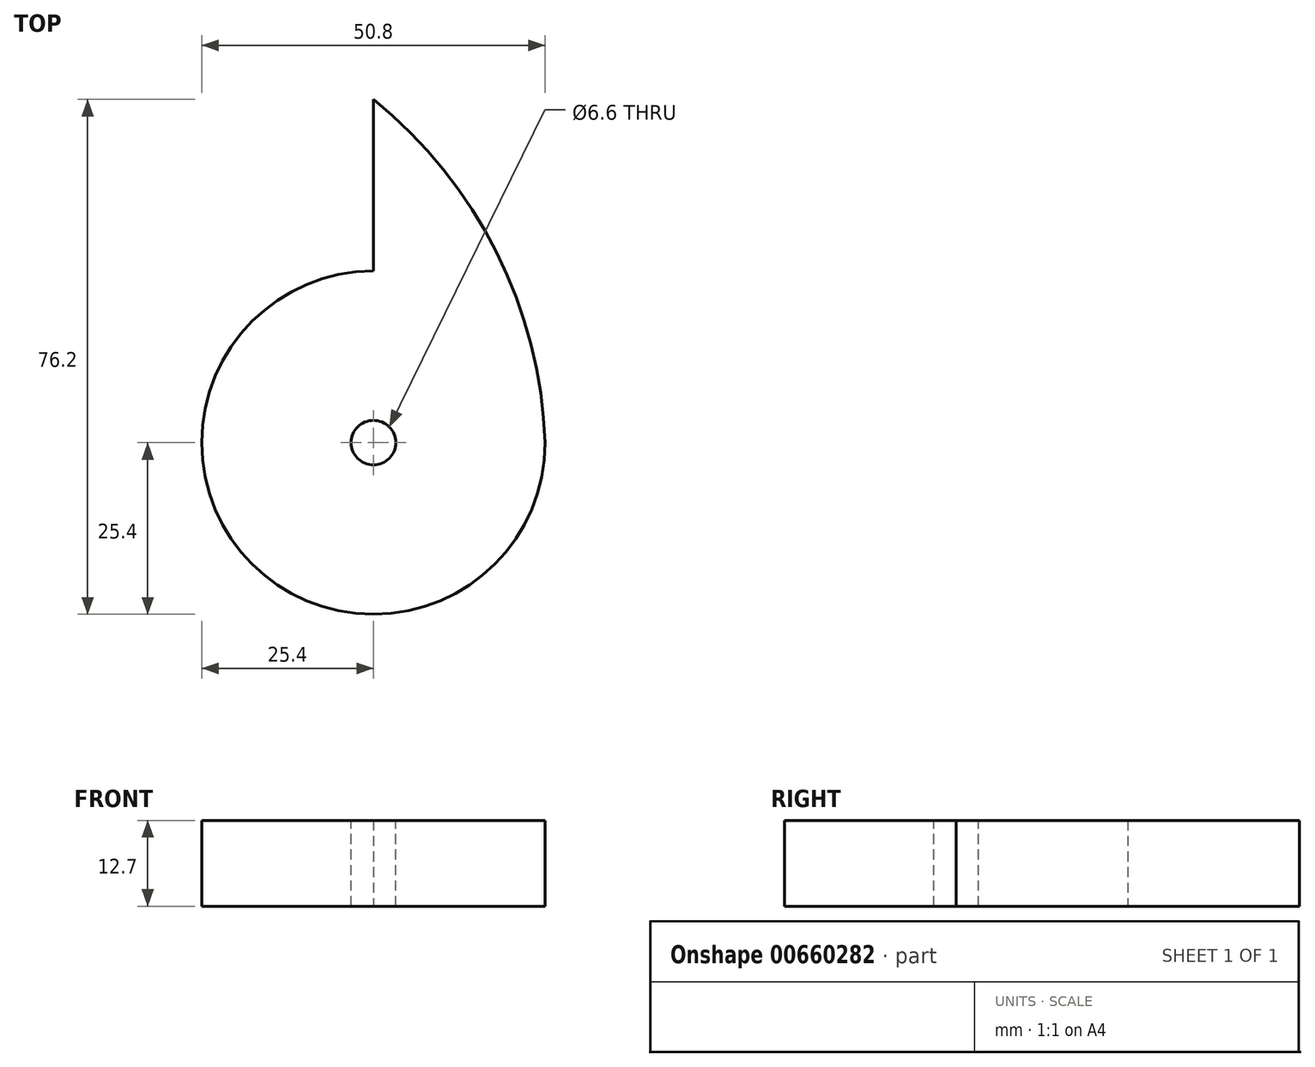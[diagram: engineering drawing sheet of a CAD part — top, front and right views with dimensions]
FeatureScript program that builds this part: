
annotation { "Feature Type Name" : "Feature", "Feature Type Description" : "" }
export const myFeature = defineFeature(function(context is Context, id is Id, definition is map)
    precondition{}
    {
        {
            var Q0;
            Q0=qCreatedBy(makeId("Top.planeOp"),FACE);
            var sketch = newSketch(context, id + "F0", { "sketchPlane" : qUnion([Q0])});
            skCircle(sketch, "E0", {"center": v(0, 0) * mm, "radius": 25.4 * mm});
            skLineSegment(sketch, "E1", {"start": v(0, 25.4) * mm, "end": v(0, 50.8) * mm});
            skArc(sketch, "E2", {"start": v(25.4, 0) * mm, "mid": v(18.21, 28.16) * mm, "end": v(0, 50.8) * mm});
            skSolve(sketch);
        }
        {
            var Q0;
            {var subQ0=sQuery(id+"F0.wireOp",EDGE,"E0");var subQ1=makeQuery(id+"F0.imprint","INTERSECT",VERTEX,{"derivedFrom":[subQ0,sQuery(id+"F0.wireOp",EDGE,"E1")]});Q0=makeQuery(id+"F0.imprint","IMPRINT",FACE,{"disambiguationData":[TD([[makeQuery(id+"F0.imprint","IMPRINT",EDGE,{"disambiguationData":[TD([[subQ1,1.0]])],"derivedFrom":subQ0}),1.0]])]});}
            var Q1;
            {var subQ0=sQuery(id+"F0.wireOp",EDGE,"E1");Q1=makeQuery(id+"F0.imprint","IMPRINT",FACE,{"disambiguationData":[TD([[makeQuery(id+"F0.imprint","IMPRINT",EDGE,{"derivedFrom":subQ0}),-1.0]])]});}
            extrude(context, id + "F1", {"entities" : qUnion([Q0, Q1]), "depth" : 12.7 * mm, "offsetDistance" : 25.4 * mm});
        }
        {
            var Q0;
            Q0=makeQuery(id+"F1.opExtrude","CAP_FACE",FACE,{"disambiguationData":[OSD([sQuery(id+"F0.wireOp",EDGE,"E0"),sQuery(id+"F0.wireOp",EDGE,"E1"),sQuery(id+"F0.wireOp",EDGE,"E2")])],"isStart":false});
            var sketch = newSketch(context, id + "F2", { "sketchPlane" : qUnion([Q0])});
            skCircle(sketch, "E3", {"center": v(0, 0) * mm, "radius": 3.3 * mm});
            skSolve(sketch);
        }
        {
            var Q0;
            Q0 = qSketchRegion(id + "F2", true);
            extrude(context, id + "F3", {"entities" : qUnion([Q0]), "operationType" : NewBodyOperationType.REMOVE, "oppositeDirection" : true, "depth" : 25.4 * mm, "offsetDistance" : 25.4 * mm});
        }
    });
